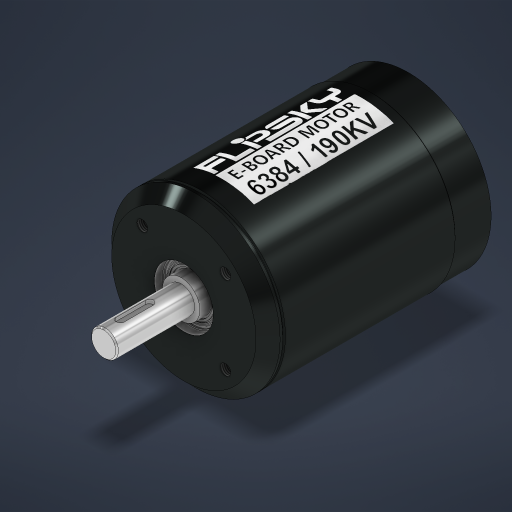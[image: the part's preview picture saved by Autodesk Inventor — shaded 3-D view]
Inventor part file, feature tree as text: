
AUTODESK INVENTOR PART (.ipt)
format: ipt  version: 2024 (Build 280153000, 153)  size: 797,184 bytes
history: native  units: in
note: dims shown in document units (in); Inventor stores cm internally (conversion verified against a paired STEP export)
features: extrude x9, sketch x9, thread x4, chamfer x2, plane x2, other x2, revolve x1, fillet x1
ambient origin geometry x8: Origin, YZ Plane, XZ Plane, XY Plane, X Axis, Y Axis, Z Axis, Center Point
bodies: Solid1 (feature_tree)
feature tree (30):
  revolve  "Revolution1"  [1 undecoded]
  extrude  "Extrusion1"  Depth=0.0394in
  thread  "Thread1"  [1 undecoded]
  thread  "Thread2"  [1 undecoded]
  thread  "Thread3"  [1 undecoded]
  thread  "Thread4"  [1 undecoded]
  extrude  "Extrusion2"  Depth=0.1575in
  chamfer  "Chamfer1"  Distance=1.5748in Angle=360.0deg
  plane  "Work Plane1"
  extrude  "Extrusion3"  Depth=0.3937in TaperAngle=0.0deg
  plane  "Work Plane2"
  other  "Decal1"
  extrude  "Extrusion4"  Depth=0.3937in TaperAngle=0.0deg
  chamfer  "Chamfer2"  Distance=0.3937in
  extrude  "Extrusion5"  Depth=1.1811in TaperAngle=0.0deg
  extrude  "Extrusion6"  Depth=0.1969in
  sketch  "Sketch9"  dims[d31=0.0197in d32=0.0787in d33=45.0deg d34=0.1969in d35=0.4331in d36=0.1181in d37=0.1575in d38=0.0591in d39=0.0in d40=1.4173in d52=0.0197in d53=0.5512in d54=0.0in d55=0.0197in d56=0.0787in d57=45.0deg d58=0.8661in d59=0.1181in d60=0.0in d61=0.5512in d62=0.1575in d63=0.0in d64=0.0197in d65=0.0276in d66=0.0394in d67=0.0197in d68=0.0in d69=0.0157in d70=0.0295in d71=0.0197in d72=0.0in d73=0.0138in d74=0.0197in d75=0.0in]
  extrude  "Extrusion7"  Depth=0.0197in
  extrude  "Extrusion8"  Depth=0.1181in
  fillet  "Fillet1"  Radius=0.1575in
  extrude  "Extrusion9"  Depth=0.0591in TaperAngle=0.0deg
  sketch  "Sketch1"  dims[d0=1.063in d1=1.2402in]
  sketch  "Sketch2"  dims[d2=45.0deg d5=0.0394in d6=0.0394in d7=0.0394in d8=0.0394in d9=3.3071in]
  sketch  "Sketch3"  dims[d10=90.0deg d11=0.1575in]
  sketch  "Sketch4"  dims[d12=0.8661in]
  sketch  "Sketch5"  dims[d13=45.0deg d14=1.5748in d16=360.0deg]
  other  "Image1"
  sketch  "Sketch6"  dims[d18=0.1969in d19=0.0in d20=0.3937in d21=0.0in]
  sketch  "Sketch7"  dims[d22=0.3937in d23=0.0in d24=0.3937in d25=0.0in d26=0.3937in d27=0.0in]
  sketch  "Sketch8"  dims[d28=0.3937in d29=1.1811in d30=0.0in]
note: 5 required parameter values undecoded (feature->parameter linkage not recoverable at this tier; creation-order binding heuristic only, values carry confidence <= 0.55)